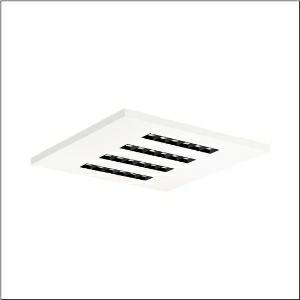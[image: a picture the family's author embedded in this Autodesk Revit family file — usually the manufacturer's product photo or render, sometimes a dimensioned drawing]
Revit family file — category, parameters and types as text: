
# Revit family: silica_r__21_square_51mx6kds44w_0efc
name_source: partatom
category: Lighting Fixtures
units: mm (PartAtom-declared; Revit-internal decimal feet)

## family parameters
Cut with Voids When Loaded = No
Host = Face
Light Source = No
Part Type = Normal
Room Calculation Point = No
Round Connector Dimension = Use Diameter
Shared = No

## types (1)
- --- (1 x LED, 4600 lm, 29.6 W, 4000K)
    Apparent Load = 30 VA
    CIE Flux Codes = 86 100 100 100 100
    Color Rendering = 80
    Color Temperature = 4000K
    Default Elevation = 1800 mm
    Description = Silica® 21 Square, office luminaire, primary light control with lens, of PMMA, primary anti-glare with reflector, of PC, black, CAT 2 (L<= 3000cd/m²), light emission: direct distribution, primary light characteristic: symmetric, installation type: lay-in mounting, LED, rated luminous flux: 4.600lm, luminous efficacy: 155lm/W, light colour: 840, colour temperature: 4000K, control gear: DALI 2, with terminal, 5-pole, mains connection: 220..240V, AC, 50/60Hz, rated input power: 29.6W, luminaire housing, of sheet steel, coated, traffic white (RAL 9016), module: M600, length: 597mm, width: 597mm, height: 33mm, protection rating (complete): IP20, insulation class (complete): insulation class I (protective earthing), certification: CE, ENEC, VDE, permissible operating ambient temperature: -20..+40°C, standard: EN 50419, packaging unit: 1 piece
    Height = 0 mm  [stored 0 ft]
    Lamp = 1 x LED
    Lamp Light Flux = 4600 lm
    Lamp Power = 29.6 W
    Lamp count = 1
    Length = 597 mm
    Luminous efficacy = 155 lm/W
    Manufacturer = Siteco
    ModVariant = No
    Model = 51MX6KDS44W
    Mounting Place = Ceiling
    Mounting Type = Recessed
    Number of Poles = 1
    OnlyDefault = Yes
    Power Factor = 1
    Product Name = Silica® 21 Square
    Product group = office luminaire | ceiling recessed
    ProductGroupID = 401
    Protection Class = Protection class I
    Protection Degree = IP 20
    RLX_Detail_Level = 1
    RLX_Emergency_Light_Flux = 0 lm
    RLX_Emergency_Type = 0
    RLX_Emergency_Type_DB = No
    RlxData = <blob elided: 21197 chars, md5=db4f17af>
    Socket = socket
    Standby Power = 0 W
    System Light Flux = 4600 lm
    System Power = 30 W
    Type Comments = factory setting: luminous flux: 100 % | dim-lin: 254 | 399 mA
    Type Image = l_1275207.jpg
    URL = http://relux.com
    VarID = @adj_084034
    Voltage = 0 V
    Weight = 0.00 kg
    Width = 597 mm

note: [stored X ft] marks values corroborated as IEEE doubles in the binary element streams (Revit-internal decimal feet)

## geometry (parser evidence)
native form markers: Blend x4, Sweep x10
no freeform markers — native parametric forms only
